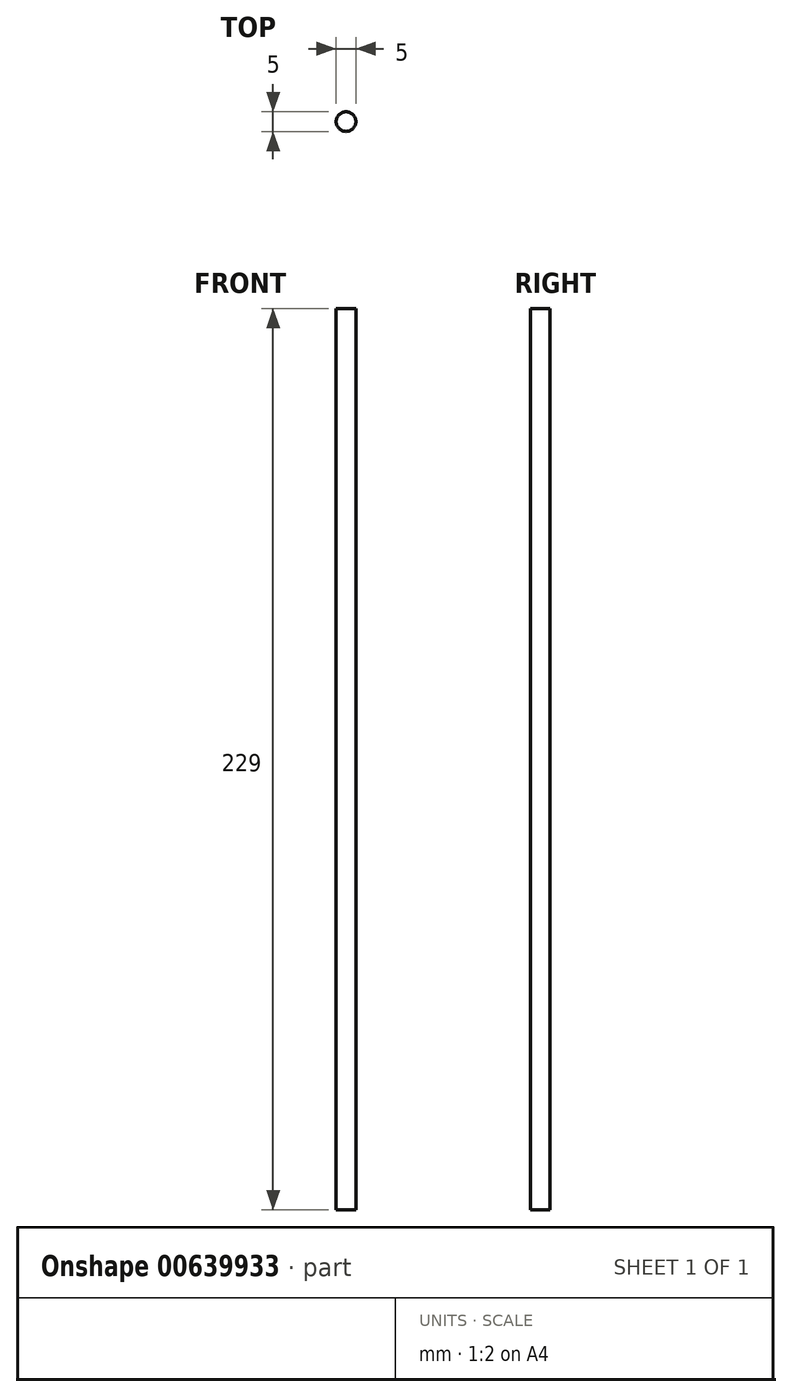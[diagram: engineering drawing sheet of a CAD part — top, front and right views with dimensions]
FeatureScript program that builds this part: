
annotation { "Feature Type Name" : "Feature", "Feature Type Description" : "" }
export const myFeature = defineFeature(function(context is Context, id is Id, definition is map)
    precondition{}
    {
        {
            var Q0;
            Q0=qCreatedBy(makeId("Top.planeOp"),FACE);
            var sketch = newSketch(context, id + "F0", { "sketchPlane" : qUnion([Q0])});
            skCircle(sketch, "E0", {"center": v(0, 0) * mm, "radius": 2.5 * mm});
            skSolve(sketch);
        }
        {
            var Q0;
            Q0=makeQuery(id+"F0.imprint","IMPRINT",FACE,{"disambiguationData":[TD([[makeQuery(id+"F0.imprint","IMPRINT",EDGE,{"derivedFrom":sQuery(id+"F0.wireOp",EDGE,"E0")}),1.0]])]});
            extrude(context, id + "F1", {"entities" : qUnion([Q0]), "depth" : 229 * mm, "offsetDistance" : 25 * mm});
        }
    });
